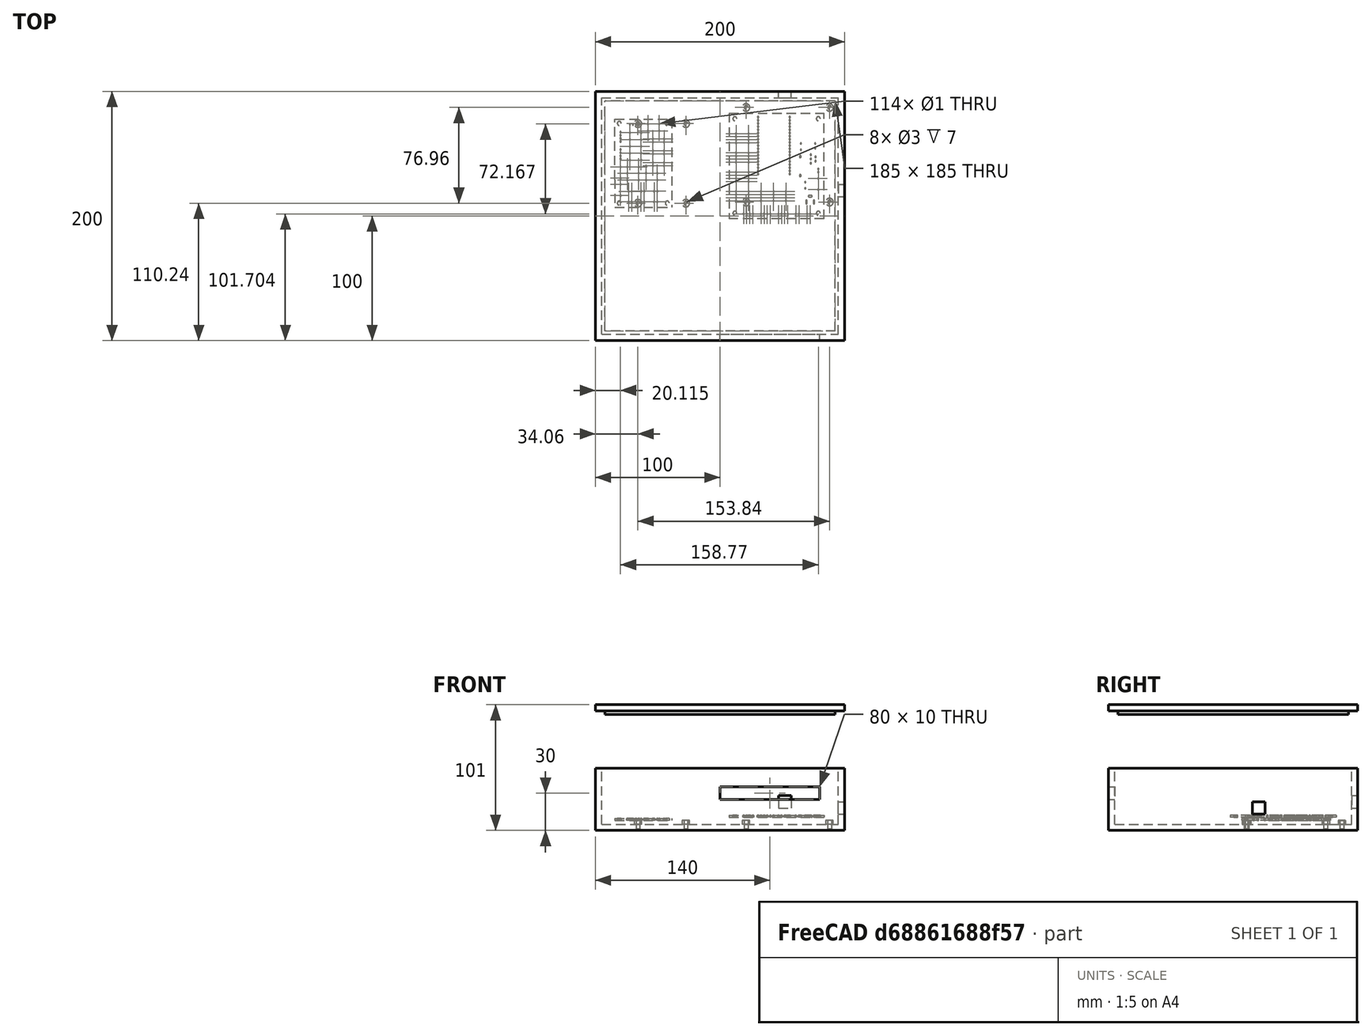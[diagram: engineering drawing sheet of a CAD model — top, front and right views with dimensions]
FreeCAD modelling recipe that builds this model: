
FCSTD DOCUMENT  (FreeCAD 0.21R33694 (Git))
Label: electronics_enclosure_v2
License: All rights reserved
LicenseURL: https://en.wikipedia.org/wiki/All_rights_reserved
objects: Part::Feature×10, Part::Cylinder×8, Part::Box×7, App::Part×6, Part::MultiFuse×4, Part::Cut×3, PartDesign::CoordinateSystem×2, Sketcher::SketchObject×2
note: 36 computed .brp shape members not serialized (recipe doc carries the construction recipe); baked Part::Feature solids carry a one-line shape summary decoded from their .brp

FEATURE [PartDesign::CoordinateSystem] Local_CS_ebcb
  AttacherType = Attacher::AttachEngine3D
  MapMode = 2
  Support = -> [X_Axis001]
FEATURE [Part::Feature] Pcb_ebcb
  Placement = pos=(-66.3846,203.371,9.60288) rot=(0,0,1;0rad)
  shape: bbox 45.5 x 71 x 1.6 mm, 75 faces (baked)
FEATURE [Sketcher::SketchObject] PCB_Sketch_ebcb
  FullyConstrained = false
  sketch-geometry (5):
    g0: LineSegment StartX=82 StartY=-96.5 StartZ=0 EndX=127.5 EndY=-96.5 EndZ=0
    g1: LineSegment StartX=82 StartY=-74 StartZ=0 EndX=82 EndY=-96.5 EndZ=0
    g2: LineSegment StartX=82 StartY=-25.5 StartZ=0 EndX=127.5 EndY=-25.5 EndZ=0
    g3: LineSegment StartX=127.5 StartY=-25.5 StartZ=0 EndX=127.5 EndY=-96.5 EndZ=0
    g4: LineSegment StartX=82 StartY=-74 StartZ=0 EndX=82 EndY=-25.5 EndZ=0
  constraints (5):
    c: Coincident(g0,g1)
    c: Coincident(g1,g4)
    c: Coincident(g2,g4)
    c: Coincident(g0,g3)
    c: Coincident(g2,g3)
FEATURE [App::Part] Board_Geoms_ebcb
  Group = -> [Pcb_ebcb,PCB_Sketch_ebcb]
  Origin = -> Origin
  Placement = pos=(6.93612,-0.134552,0.200878) rot=(0,0,1;0rad)
FEATURE [App::Part] Step_Models_ebcb
  Origin = -> Origin002
FEATURE [App::Part] Board_ebcb  label="ir_sensor"
  Group = -> [Local_CS_ebcb,Board_Geoms_ebcb,Step_Models_ebcb]
  Origin = -> Origin001
  Placement = pos=(8,0,0) rot=(0,0,1;0rad)
FEATURE [PartDesign::CoordinateSystem] Local_CS_b27c
  AttacherType = Attacher::AttachEngine3D
  MapMode = 2
  Support = -> [X_Axis004]
FEATURE [Part::Feature] Pcb_b27c
  Placement = pos=(-27.615,242.704,12.0679) rot=(0,0,1;0rad)
  shape: bbox 76 x 85 x 1.6 mm, 143 faces (baked)
FEATURE [Sketcher::SketchObject] PCB_Sketch_b27c
  FullyConstrained = false
  sketch-geometry (4):
    g0: LineSegment StartX=211 StartY=-145 StartZ=0 EndX=211 EndY=-60 EndZ=0
    g1: LineSegment StartX=135 StartY=-60 StartZ=0 EndX=135 EndY=-145 EndZ=0
    g2: LineSegment StartX=211 StartY=-145 StartZ=0 EndX=135 EndY=-145 EndZ=0
    g3: LineSegment StartX=135 StartY=-60 StartZ=0 EndX=211 EndY=-60 EndZ=0
  constraints (4):
    c: Coincident(g1,g2)
    c: Coincident(g1,g3)
    c: Coincident(g0,g2)
    c: Coincident(g0,g3)
FEATURE [App::Part] Board_Geoms_b27c
  Group = -> [Pcb_b27c,PCB_Sketch_b27c]
  Origin = -> Origin003
FEATURE [App::Part] Step_Models_b27c
  Origin = -> Origin005
FEATURE [App::Part] Board_b27c  label="beehive"
  Group = -> [Local_CS_b27c,Board_Geoms_b27c,Step_Models_b27c]
  Origin = -> Origin004
  Placement = pos=(9,9,-2) rot=(0,0,1;0rad)
FEATURE [Part::Box] Box  label="Cube"
  AttacherType = Attacher::AttachEngine3D
  Height = 50
  Length = 200
  Width = 200
FEATURE [Part::Box] Box001  label="Cube001"
  AttacherType = Attacher::AttachEngine3D
  Height = 45
  Length = 190
  Placement = pos=(5,5,5) rot=(0,0,1;0rad)
  Width = 190
FEATURE [Part::Cut] Cut
  Base = -> Box
  Tool = -> Box001
FEATURE [Part::Cylinder] Cylinder
  Angle = 360
  AttacherType = Attacher::AttachEngine3D
  FirstAngle = 0
  Height = 8
  Placement = pos=(120.9,111.2,0) rot=(0,0,1;0rad)
  Radius = 3
  SecondAngle = 0
FEATURE [Part::Cylinder] Cylinder001
  Angle = 360
  AttacherType = Attacher::AttachEngine3D
  FirstAngle = 0
  Height = 8
  Placement = pos=(120.9,187.2,0) rot=(0,0,1;0rad)
  Radius = 3
  SecondAngle = 0
FEATURE [Part::Cylinder] Cylinder002
  Angle = 360
  AttacherType = Attacher::AttachEngine3D
  FirstAngle = 0
  Height = 8
  Placement = pos=(187.9,187.2,0) rot=(0,0,1;0rad)
  Radius = 3
  SecondAngle = 0
FEATURE [Part::Cylinder] Cylinder003
  Angle = 360
  AttacherType = Attacher::AttachEngine3D
  FirstAngle = 0
  Height = 8
  Placement = pos=(187.9,111.2,0) rot=(0,0,1;0rad)
  Radius = 3
  SecondAngle = 0
FEATURE [Part::Cylinder] Cylinder004
  Angle = 360
  AttacherType = Attacher::AttachEngine3D
  FirstAngle = 0
  Height = 8
  Placement = pos=(72.56,110.24,0) rot=(0,0,1;0rad)
  Radius = 3
  SecondAngle = 0
FEATURE [Part::Cylinder] Cylinder005
  Angle = 360
  AttacherType = Attacher::AttachEngine3D
  FirstAngle = 0
  Height = 8
  Placement = pos=(72.56,174.24,0) rot=(0,0,1;0rad)
  Radius = 3
  SecondAngle = 0
FEATURE [Part::Cylinder] Cylinder006
  Angle = 360
  AttacherType = Attacher::AttachEngine3D
  FirstAngle = 0
  Height = 8
  Placement = pos=(34.06,174.24,0) rot=(0,0,1;0rad)
  Radius = 3
  SecondAngle = 0
FEATURE [Part::Cylinder] Cylinder007
  Angle = 360
  AttacherType = Attacher::AttachEngine3D
  FirstAngle = 0
  Height = 8
  Placement = pos=(34.06,110.24,0) rot=(0,0,1;0rad)
  Radius = 3
  SecondAngle = 0
FEATURE [Part::Box] Box002  label="Cube002"
  AttacherType = Attacher::AttachEngine3D
  Height = 10
  Length = 10
  Placement = pos=(147,190.5,18) rot=(0,0,1;0rad)
  Width = 10
FEATURE [Part::Box] Box003  label="Cube003"
  AttacherType = Attacher::AttachEngine3D
  Height = 10
  Length = 10
  Placement = pos=(191,115.5,13) rot=(0,0,1;0rad)
  Width = 10
FEATURE [Part::Box] Box004  label="Cube004"
  AttacherType = Attacher::AttachEngine3D
  Height = 10
  Length = 80
  Placement = pos=(100,-1,25) rot=(0,0,1;0rad)
  Width = 10
FEATURE [Part::MultiFuse] Fusion
  Shapes = -> [Box002,Box003,Box004]
FEATURE [Part::Cut] Cut001
  Base = -> Cut
  Tool = -> Fusion
FEATURE [Part::MultiFuse] Fusion001  label="box_bottom"
  Shapes = -> [Cut001,Cylinder007,Cylinder006,Cylinder005,Cylinder004,Cylinder003,Cylinder002,Cylinder001,Cylinder]
FEATURE [Part::Box] Box005  label="Cube005"
  AttacherType = Attacher::AttachEngine3D
  Height = 5
  Length = 200
  Placement = pos=(0,0,96) rot=(0,0,1;0rad)
  Width = 200
FEATURE [Part::Box] Box006  label="Cube006"
  AttacherType = Attacher::AttachEngine3D
  Height = 8
  Length = 185
  Placement = pos=(7.5,7.5,93) rot=(0,0,1;0rad)
  Width = 185
FEATURE [Part::MultiFuse] Fusion002  label="lid"
  Shapes = -> [Box005,Box006]
FEATURE [Part::Feature] BOLTS_part  label="Hexagon head bolt M3 - 10.0"
  Placement = pos=(187.9,187.2,13) rot=(1,0,0;3.14159rad)
  shape: bbox 5.5 x 6.351 x 12 mm, 11 faces (baked)
FEATURE [Part::Feature] BOLTS_part001  label="Hexagon head bolt M3 - 10.001"
  Placement = pos=(187.9,111.2,13) rot=(1,0,0;3.14159rad)
  shape: bbox 5.5 x 6.351 x 12 mm, 11 faces (baked)
FEATURE [Part::Feature] BOLTS_part002  label="Hexagon head bolt M3 - 10.002"
  Placement = pos=(120.9,111.2,13) rot=(1,0,0;3.14159rad)
  shape: bbox 5.5 x 6.351 x 12 mm, 11 faces (baked)
FEATURE [Part::Feature] BOLTS_part003  label="Hexagon head bolt M3 - 10.003"
  Placement = pos=(120.9,187.2,13) rot=(1,0,0;3.14159rad)
  shape: bbox 5.5 x 6.351 x 12 mm, 11 faces (baked)
FEATURE [Part::Feature] BOLTS_part004  label="Hexagon head bolt M3 - 10.004"
  Placement = pos=(72.56,110.24,13) rot=(1,0,0;3.14159rad)
  shape: bbox 5.5 x 6.351 x 12 mm, 11 faces (baked)
FEATURE [Part::Feature] BOLTS_part005  label="Hexagon head bolt M3 - 10.005"
  Placement = pos=(34.06,174.24,13) rot=(1,0,0;3.14159rad)
  shape: bbox 5.5 x 6.351 x 12 mm, 11 faces (baked)
FEATURE [Part::Feature] BOLTS_part006  label="Hexagon head bolt M3 - 10.006"
  Placement = pos=(72.56,174.24,13) rot=(1,0,0;3.14159rad)
  shape: bbox 5.5 x 6.351 x 12 mm, 11 faces (baked)
FEATURE [Part::Feature] BOLTS_part007  label="Hexagon head bolt M3 - 10.007"
  Placement = pos=(34.06,110.24,13) rot=(1,0,0;3.14159rad)
  shape: bbox 5.5 x 6.351 x 12 mm, 11 faces (baked)
FEATURE [Part::MultiFuse] Fusion003  label="screws"
  Shapes = -> [BOLTS_part,BOLTS_part001,BOLTS_part002,BOLTS_part003,BOLTS_part004,BOLTS_part005,BOLTS_part006,BOLTS_part007]
FEATURE [Part::Cut] Cut002
  Base = -> Fusion001
  Tool = -> Fusion003
